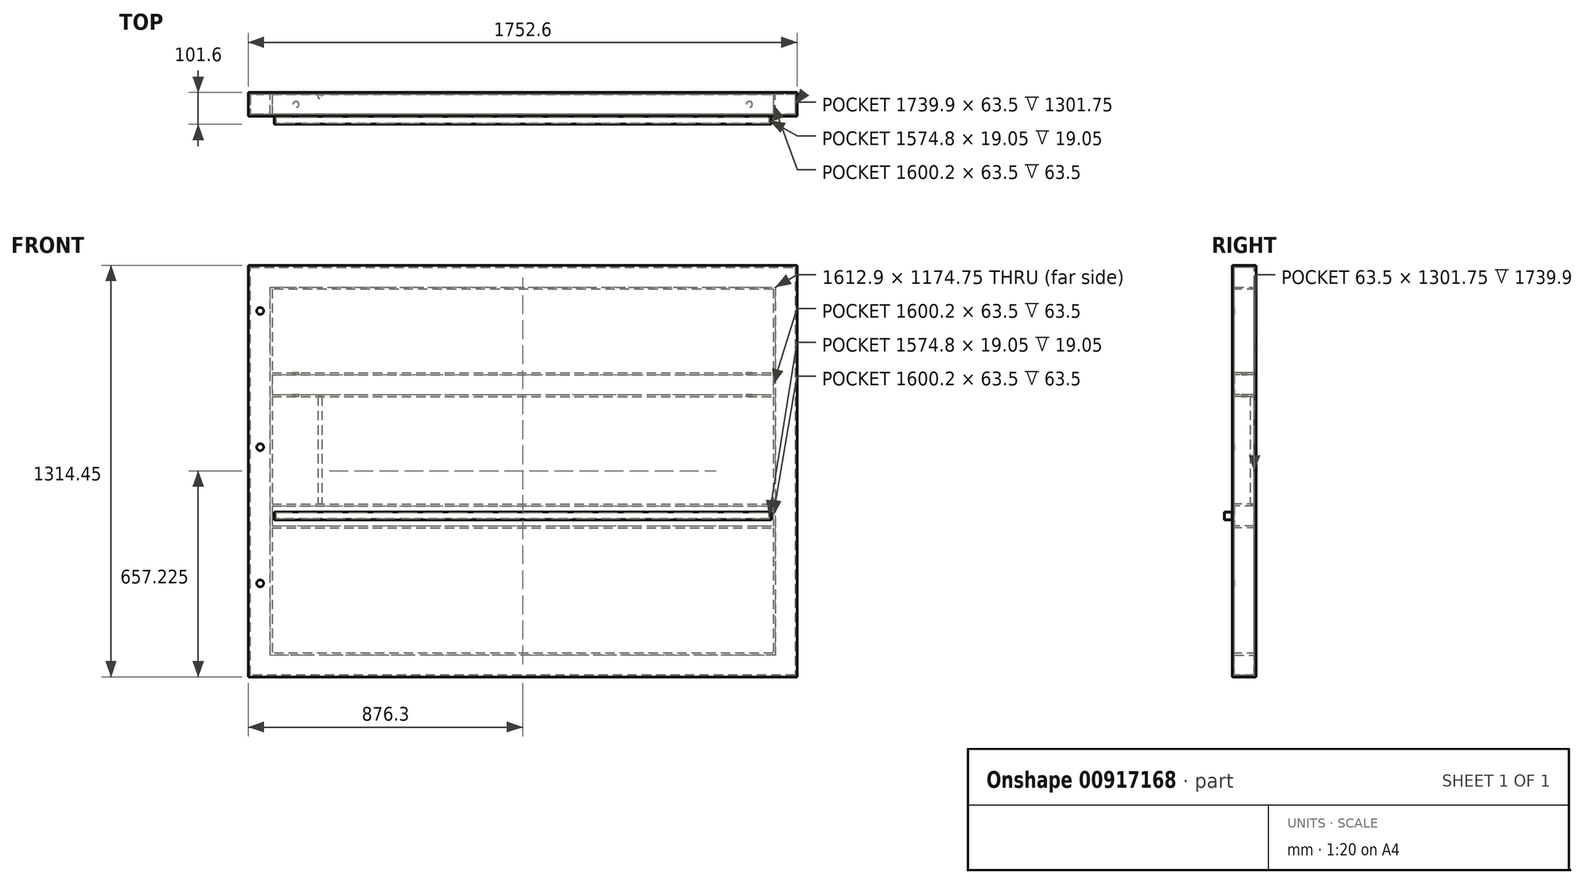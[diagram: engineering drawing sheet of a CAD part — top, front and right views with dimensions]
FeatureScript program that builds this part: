
annotation { "Feature Type Name" : "Feature", "Feature Type Description" : "" }
export const myFeature = defineFeature(function(context is Context, id is Id, definition is map)
    precondition{}
    {
        {
            var Q0;
            Q0=qCreatedBy(makeId("Front.planeOp"),FACE);
            var sketch = newSketch(context, id + "F0", { "sketchPlane" : qUnion([Q0])});
            skLineSegment(sketch, "E0.bottom", {"start": v(-876.3, 660.4) * mm, "end": v(876.3, 660.4) * mm});
            skLineSegment(sketch, "E0.top", {"start": v(-876.3, -654.05) * mm, "end": v(876.3, -654.05) * mm});
            skLineSegment(sketch, "E0.left", {"start": v(-876.3, 660.4) * mm, "end": v(-876.3, -654.05) * mm});
            skLineSegment(sketch, "E0.right", {"start": v(876.3, 660.4) * mm, "end": v(876.3, -654.05) * mm});
            skLineSegment(sketch, "E1.bottom", {"start": v(-800.1, 635) * mm, "end": v(800.1, 635) * mm, "construction": true});
            skLineSegment(sketch, "E1.top", {"start": v(-800.1, -603.25) * mm, "end": v(800.1, -603.25) * mm, "construction": true});
            skLineSegment(sketch, "E1.left", {"start": v(-800.1, 635) * mm, "end": v(-800.1, -603.25) * mm, "construction": true});
            skLineSegment(sketch, "E1.right", {"start": v(800.1, 635) * mm, "end": v(800.1, -603.25) * mm, "construction": true});
            skSolve(sketch);
        }
        {
            var Q0;
            Q0=qCreatedBy(makeId("Top.planeOp"),FACE);
            var sketch = newSketch(context, id + "F1", { "sketchPlane" : qUnion([Q0])});
            skLineSegment(sketch, "E2.bottom", {"start": v(-800.1, -76.2) * mm, "end": v(-876.3, -76.2) * mm});
            skLineSegment(sketch, "E2.top", {"start": v(-800.1, 0) * mm, "end": v(-876.3, 0) * mm});
            skLineSegment(sketch, "E2.left", {"start": v(-800.1, -76.2) * mm, "end": v(-800.1, 0) * mm});
            skLineSegment(sketch, "E2.right", {"start": v(-876.3, -76.2) * mm, "end": v(-876.3, 0) * mm});
            skPoint(sketch, "E2.middle", {"position": v(-838.2, -38.1) * mm});
            skLineSegment(sketch, "E3.bottom", {"start": v(-806.45, -69.85) * mm, "end": v(-869.95, -69.85) * mm});
            skLineSegment(sketch, "E3.top", {"start": v(-806.45, -6.35) * mm, "end": v(-869.95, -6.35) * mm});
            skLineSegment(sketch, "E3.left", {"start": v(-806.45, -69.85) * mm, "end": v(-806.45, -6.35) * mm});
            skLineSegment(sketch, "E3.right", {"start": v(-869.95, -69.85) * mm, "end": v(-869.95, -6.35) * mm});
            skSolve(sketch);
        }
        {
            var Q0;
            Q0=qSketchRegion(id+"F1",true);
            var Q1;
            Q1=qConstructionFilter(qBodyType(qCreatedBy(id+"F0",EDGE),BodyType.WIRE),ConstructionObject.NO);
            sweep(context, id + "F2", {"profiles" : qUnion([Q0]), "path" : qUnion([Q1])});
        }
        {
            var Q0;
            Q0=qCreatedBy(makeId("Right.planeOp"),FACE);
            var sketch = newSketch(context, id + "F3", { "sketchPlane" : qUnion([Q0])});
            skLineSegment(sketch, "E4.bottom", {"start": v(0, 736.6) * mm, "end": v(-76.2, 736.6) * mm, "construction": true});
            skLineSegment(sketch, "E4.top", {"start": v(0, 660.4) * mm, "end": v(-76.2, 660.4) * mm, "construction": true});
            skLineSegment(sketch, "E4.left", {"start": v(0, 736.6) * mm, "end": v(0, 660.4) * mm, "construction": true});
            skLineSegment(sketch, "E4.right", {"start": v(-76.2, 736.6) * mm, "end": v(-76.2, 660.4) * mm, "construction": true});
            skPoint(sketch, "E4.middle", {"position": v(-38.1, 698.5) * mm});
            skLineSegment(sketch, "E5.bottom", {"start": v(-6.35, 730.25) * mm, "end": v(-69.85, 730.25) * mm, "construction": true});
            skLineSegment(sketch, "E5.top", {"start": v(-6.35, 666.75) * mm, "end": v(-69.85, 666.75) * mm, "construction": true});
            skLineSegment(sketch, "E5.left", {"start": v(-6.35, 730.25) * mm, "end": v(-6.35, 666.75) * mm, "construction": true});
            skLineSegment(sketch, "E5.right", {"start": v(-69.85, 730.25) * mm, "end": v(-69.85, 666.75) * mm, "construction": true});
            skLineSegment(sketch, "E6.0.1.0", {"start": v(0, 317.5) * mm, "end": v(-76.2, 317.5) * mm});
            skLineSegment(sketch, "E6.0.1.1", {"start": v(0, 241.3) * mm, "end": v(-76.2, 241.3) * mm});
            skLineSegment(sketch, "E6.0.1.2", {"start": v(0, 317.5) * mm, "end": v(0, 241.3) * mm});
            skLineSegment(sketch, "E6.0.1.3", {"start": v(-76.2, 317.5) * mm, "end": v(-76.2, 241.3) * mm});
            skLineSegment(sketch, "E6.0.1.4", {"start": v(-6.35, 311.15) * mm, "end": v(-69.85, 311.15) * mm});
            skLineSegment(sketch, "E6.0.1.5", {"start": v(-6.35, 247.65) * mm, "end": v(-69.85, 247.65) * mm});
            skLineSegment(sketch, "E6.0.1.6", {"start": v(-6.35, 311.15) * mm, "end": v(-6.35, 247.65) * mm});
            skLineSegment(sketch, "E6.0.1.7", {"start": v(-69.85, 311.15) * mm, "end": v(-69.85, 247.65) * mm});
            skPoint(sketch, "E6.0.1.8", {"position": v(-38.1, 279.4) * mm});
            skPoint(sketch, "E6.0.1.9", {"position": v(-38.1, 279.4) * mm});
            skLineSegment(sketch, "E6.direction1", {"start": v(-76.2, 660.4) * mm, "end": v(586.54, 660.4) * mm, "construction": true});
            skLineSegment(sketch, "E6.direction2", {"start": v(-76.2, 660.4) * mm, "end": v(-76.2, 241.3) * mm, "construction": true});
            skLineSegment(sketch, "E7.0.0.2", {"start": v(0, -101.6) * mm, "end": v(-76.2, -101.6) * mm});
            skLineSegment(sketch, "E7.3.0.2", {"start": v(0, -177.8) * mm, "end": v(-76.2, -177.8) * mm});
            skLineSegment(sketch, "E7.6.0.2", {"start": v(0, -101.6) * mm, "end": v(0, -177.8) * mm});
            skLineSegment(sketch, "E7.9.0.2", {"start": v(-76.2, -101.6) * mm, "end": v(-76.2, -177.8) * mm});
            skLineSegment(sketch, "E7.12.0.2", {"start": v(-6.35, -107.95) * mm, "end": v(-69.85, -107.95) * mm});
            skLineSegment(sketch, "E7.15.0.2", {"start": v(-6.35, -171.45) * mm, "end": v(-69.85, -171.45) * mm});
            skLineSegment(sketch, "E7.18.0.2", {"start": v(-6.35, -107.95) * mm, "end": v(-6.35, -171.45) * mm});
            skLineSegment(sketch, "E7.21.0.2", {"start": v(-69.85, -107.95) * mm, "end": v(-69.85, -171.45) * mm});
            skPoint(sketch, "E7.24.0.2", {"position": v(-38.1, -139.7) * mm});
            skPoint(sketch, "E7.25.0.2", {"position": v(-38.1, -139.7) * mm});
            skLineSegment(sketch, "E8.0.0.3", {"start": v(0, -520.7) * mm, "end": v(-76.2, -520.7) * mm, "construction": true});
            skLineSegment(sketch, "E8.3.0.3", {"start": v(0, -596.9) * mm, "end": v(-76.2, -596.9) * mm, "construction": true});
            skLineSegment(sketch, "E8.6.0.3", {"start": v(0, -520.7) * mm, "end": v(0, -596.9) * mm, "construction": true});
            skLineSegment(sketch, "E8.9.0.3", {"start": v(-76.2, -520.7) * mm, "end": v(-76.2, -596.9) * mm, "construction": true});
            skLineSegment(sketch, "E8.12.0.3", {"start": v(-6.35, -527.05) * mm, "end": v(-69.85, -527.05) * mm, "construction": true});
            skLineSegment(sketch, "E8.15.0.3", {"start": v(-6.35, -590.55) * mm, "end": v(-69.85, -590.55) * mm, "construction": true});
            skLineSegment(sketch, "E8.18.0.3", {"start": v(-6.35, -527.05) * mm, "end": v(-6.35, -590.55) * mm, "construction": true});
            skLineSegment(sketch, "E8.21.0.3", {"start": v(-69.85, -527.05) * mm, "end": v(-69.85, -590.55) * mm, "construction": true});
            skPoint(sketch, "E8.24.0.3", {"position": v(-38.1, -558.8) * mm});
            skPoint(sketch, "E8.25.0.3", {"position": v(-38.1, -558.8) * mm});
            skLineSegment(sketch, "E9", {"start": v(-76.2, -673.1) * mm, "end": v(-76.2, -520.7) * mm, "construction": true});
            skLineSegment(sketch, "E10", {"start": v(-76.2, -520.7) * mm, "end": v(0, -520.7) * mm, "construction": true});
            skLineSegment(sketch, "E11", {"start": v(0, -520.7) * mm, "end": v(0, -527.05) * mm, "construction": true});
            skLineSegment(sketch, "E12", {"start": v(0, -527.05) * mm, "end": v(-69.85, -527.05) * mm, "construction": true});
            skLineSegment(sketch, "E13", {"start": v(-69.85, -527.05) * mm, "end": v(-69.85, -666.75) * mm, "construction": true});
            skLineSegment(sketch, "E14", {"start": v(-69.85, -666.75) * mm, "end": v(0, -666.75) * mm, "construction": true});
            skLineSegment(sketch, "E15", {"start": v(0, -666.75) * mm, "end": v(0, -673.1) * mm, "construction": true});
            skLineSegment(sketch, "E16", {"start": v(-76.2, -673.1) * mm, "end": v(0, -673.1) * mm, "construction": true});
            skLineSegment(sketch, "E17", {"start": v(-38.1, 660.4) * mm, "end": v(-38.1, 317.5) * mm, "construction": true});
            skLineSegment(sketch, "E18", {"start": v(-38.1, 317.5) * mm, "end": v(-38.1, 241.3) * mm, "construction": true});
            skLineSegment(sketch, "E19", {"start": v(-38.1, 241.3) * mm, "end": v(-38.1, -101.6) * mm, "construction": true});
            skLineSegment(sketch, "E20", {"start": v(-38.1, -101.6) * mm, "end": v(-38.1, -177.8) * mm, "construction": true});
            skLineSegment(sketch, "E21", {"start": v(-38.1, -177.8) * mm, "end": v(-38.1, -520.7) * mm, "construction": true});
            skLineSegment(sketch, "E22.bottom", {"start": v(-76.2, -596.9) * mm, "end": v(0, -596.9) * mm, "construction": true});
            skLineSegment(sketch, "E22.left", {"start": v(-76.2, -596.9) * mm, "end": v(-76.2, -673.1) * mm, "construction": true});
            skLineSegment(sketch, "E22.right", {"start": v(0, -596.9) * mm, "end": v(0, -673.1) * mm, "construction": true});
            skPoint(sketch, "E22.middle", {"position": v(-38.1, -635) * mm});
            skLineSegment(sketch, "E23.bottom", {"start": v(-6.35, -603.25) * mm, "end": v(-69.85, -603.25) * mm, "construction": true});
            skLineSegment(sketch, "E23.top", {"start": v(-6.35, -666.75) * mm, "end": v(-69.85, -666.75) * mm, "construction": true});
            skLineSegment(sketch, "E23.left", {"start": v(-6.35, -603.25) * mm, "end": v(-6.35, -666.75) * mm, "construction": true});
            skLineSegment(sketch, "E23.right", {"start": v(-69.85, -603.25) * mm, "end": v(-69.85, -666.75) * mm, "construction": true});
            skSolve(sketch);
        }
        {
            var Q0;
            Q0=qSketchRegion(id+"F3",true);
            var Q1;
            Q1=makeQuery(id+"F2.opSweep","SWEPT_FACE",FACE,{"disambiguationData":[OSD([sQuery(id+"F0.wireOp",EDGE,"E0.left"),sQuery(id+"F1.wireOp",EDGE,"E2.left")])]});
            var Q2;
            Q2=makeQuery(id+"F2.opSweep","CAP_VERTEX",VERTEX,{"disambiguationData":[OSD([sQuery(id+"F0.wireOp",EDGE,"E0.bottom"),sQuery(id+"F1.wireOp",EDGE,"E2.bottom"),sQuery(id+"F1.wireOp",EDGE,"E2.left")])],"isStart":true});
            var Q3;
            Q3=makeQuery(id+"F2.opSweep","SWEPT_FACE",FACE,{"disambiguationData":[OSD([sQuery(id+"F0.wireOp",EDGE,"E0.right"),sQuery(id+"F1.wireOp",EDGE,"E2.left")])]});
            var Q4;
            Q4=makeQuery(id+"F2.opSweep","MID_CAP_VERTEX",VERTEX,{"disambiguationData":[OSD([sQuery(id+"F0.wireOp",EDGE,"E0.bottom"),sQuery(id+"F1.wireOp",EDGE,"E2.bottom"),sQuery(id+"F1.wireOp",EDGE,"E2.left")])],"capPos":1.0});
            extrude(context, id + "F4", {"entities" : qUnion([Q0]), "operationType" : NewBodyOperationType.ADD, "endBound" : BoundingType.UP_TO_VERTEX, "oppositeDirection" : true, "depth" : 25.4 * mm, "endBoundEntityFace" : qUnion([Q1]), "endBoundEntityVertex" : qUnion([Q2]), "offsetDistance" : 25.4 * mm, "hasSecondDirection" : true, "secondDirectionBound" : SecondDirectionBoundingType.UP_TO_VERTEX, "secondDirectionOppositeDirection" : false, "secondDirectionDepth" : 25.4 * mm, "secondDirectionBoundEntityFace" : qUnion([Q3]), "secondDirectionBoundEntityVertex" : qUnion([Q4])});
        }
        {
            var Q0;
            Q0=qCreatedBy(makeId("Right.planeOp"),FACE);
            var sketch = newSketch(context, id + "F5", { "sketchPlane" : qUnion([Q0])});
            skLineSegment(sketch, "E24.bottom", {"start": v(-76.2, -127) * mm, "end": v(-101.6, -127) * mm});
            skLineSegment(sketch, "E24.top", {"start": v(-76.2, -152.4) * mm, "end": v(-101.6, -152.4) * mm});
            skLineSegment(sketch, "E24.left", {"start": v(-76.2, -127) * mm, "end": v(-76.2, -152.4) * mm});
            skLineSegment(sketch, "E24.right", {"start": v(-101.6, -127) * mm, "end": v(-101.6, -152.4) * mm});
            skPoint(sketch, "E24.middle", {"position": v(-88.9, -139.7) * mm});
            skLineSegment(sketch, "E25.bottom", {"start": v(-79.37, -130.17) * mm, "end": v(-98.42, -130.17) * mm});
            skLineSegment(sketch, "E25.top", {"start": v(-79.37, -149.22) * mm, "end": v(-98.42, -149.22) * mm});
            skLineSegment(sketch, "E25.left", {"start": v(-79.37, -130.17) * mm, "end": v(-79.37, -149.22) * mm});
            skLineSegment(sketch, "E25.right", {"start": v(-98.42, -130.17) * mm, "end": v(-98.42, -149.22) * mm});
            skSolve(sketch);
        }
        {
            var Q0;
            Q0=qSketchRegion(id+"F5",true);
            extrude(context, id + "F6", {"entities" : qUnion([Q0]), "operationType" : NewBodyOperationType.ADD, "endBound" : BoundingType.SYMMETRIC, "depth" : 1587.5 * mm, "offsetDistance" : 25.4 * mm});
        }
        {
            var Q0;
            Q0=makeQuery(id+"F6.opExtrude","SWEPT_FACE",FACE,{"disambiguationData":[OSD([sQuery(id+"F5.wireOp",EDGE,"E24.bottom")])]});
            var sketch = newSketch(context, id + "F7", { "sketchPlane" : qUnion([Q0])});
            skLineSegment(sketch, "E26.bottom", {"start": v(793.75, -76.2) * mm, "end": v(787.4, -76.2) * mm});
            skLineSegment(sketch, "E26.top", {"start": v(793.75, -101.6) * mm, "end": v(787.4, -101.6) * mm});
            skLineSegment(sketch, "E26.left", {"start": v(793.75, -76.2) * mm, "end": v(793.75, -101.6) * mm});
            skLineSegment(sketch, "E26.right", {"start": v(787.4, -76.2) * mm, "end": v(787.4, -101.6) * mm});
            skLineSegment(sketch, "E27.bottom", {"start": v(-793.75, -76.2) * mm, "end": v(-787.4, -76.2) * mm});
            skLineSegment(sketch, "E27.top", {"start": v(-793.75, -101.6) * mm, "end": v(-787.4, -101.6) * mm});
            skLineSegment(sketch, "E27.left", {"start": v(-793.75, -76.2) * mm, "end": v(-793.75, -101.6) * mm});
            skLineSegment(sketch, "E27.right", {"start": v(-787.4, -76.2) * mm, "end": v(-787.4, -101.6) * mm});
            skSolve(sketch);
        }
        {
            var Q0;
            Q0=qSketchRegion(id+"F7",true);
            var Q1;
            Q1=makeQuery(id+"F6.opExtrude","CAP_VERTEX",VERTEX,{"disambiguationData":[OSD([sQuery(id+"F5.wireOp",EDGE,"E24.top"),sQuery(id+"F5.wireOp",EDGE,"E24.right")])],"isStart":false});
            extrude(context, id + "F8", {"entities" : qUnion([Q0]), "operationType" : NewBodyOperationType.ADD, "endBound" : BoundingType.UP_TO_VERTEX, "oppositeDirection" : true, "depth" : 25.4 * mm, "endBoundEntityVertex" : qUnion([Q1]), "offsetDistance" : 25.4 * mm});
        }
        {
            var Q0;
            Q0=qCreatedBy(makeId("Top.planeOp"),FACE);
            var sketch = newSketch(context, id + "F9", { "sketchPlane" : qUnion([Q0])});
            skLineSegment(sketch, "E28.bottom", {"start": v(800.1, -76.2) * mm, "end": v(-800.1, -76.2) * mm});
            skLineSegment(sketch, "E28.top", {"start": v(800.1, -73.53) * mm, "end": v(-800.1, -73.53) * mm});
            skLineSegment(sketch, "E28.left", {"start": v(800.1, -76.2) * mm, "end": v(800.1, -73.53) * mm});
            skLineSegment(sketch, "E28.right", {"start": v(-800.1, -76.2) * mm, "end": v(-800.1, -73.53) * mm});
            skPoint(sketch, "E28.middle", {"position": v(0, -74.87) * mm});
            skSolve(sketch);
        }
        {
            var Q0;
            Q0=qSketchRegion(id+"F9",true);
            var Q1;
            Q1=makeQuery(id+"F2.opSweep","CAP_VERTEX",VERTEX,{"disambiguationData":[OSD([sQuery(id+"F0.wireOp",EDGE,"E0.bottom"),sQuery(id+"F1.wireOp",EDGE,"E2.top"),sQuery(id+"F1.wireOp",EDGE,"E2.left")])],"isStart":true});
            var Q2;
            Q2=makeQuery(id+"F2.opSweep","MID_CAP_VERTEX",VERTEX,{"disambiguationData":[OSD([sQuery(id+"F0.wireOp",EDGE,"E0.left"),sQuery(id+"F1.wireOp",EDGE,"E2.top"),sQuery(id+"F1.wireOp",EDGE,"E2.left")])],"capPos":3.0});
            extrude(context, id + "F10", {"entities" : qUnion([Q0]), "operationType" : NewBodyOperationType.ADD, "endBound" : BoundingType.UP_TO_VERTEX, "depth" : 25.4 * mm, "endBoundEntityVertex" : qUnion([Q1]), "offsetDistance" : 25.4 * mm, "hasSecondDirection" : true, "secondDirectionBound" : SecondDirectionBoundingType.UP_TO_VERTEX, "secondDirectionOppositeDirection" : true, "secondDirectionDepth" : 25.4 * mm, "secondDirectionBoundEntityVertex" : qUnion([Q2])});
        }
        {
            var Q0;
            Q0=qCreatedBy(makeId("Front.planeOp"),FACE);
            var sketch = newSketch(context, id + "F11", { "sketchPlane" : qUnion([Q0])});
            skCircle(sketch, "E29", {"center": v(-838.2, 514.35) * mm, "radius": 11.11 * mm});
            skCircle(sketch, "E30", {"center": v(-838.2, 79.37) * mm, "radius": 11.11 * mm});
            skCircle(sketch, "E31", {"center": v(-838.2, -355.6) * mm, "radius": 11.11 * mm});
            skLineSegment(sketch, "E32", {"start": v(-838.2, 79.37) * mm, "end": v(-838.2, -355.6) * mm, "construction": true});
            skLineSegment(sketch, "E33", {"start": v(-838.2, 514.35) * mm, "end": v(-838.2, 79.37) * mm, "construction": true});
            skLineSegment(sketch, "E34", {"start": v(-838.2, 660.4) * mm, "end": v(-838.2, 514.35) * mm, "construction": true});
            skLineSegment(sketch, "E35", {"start": v(-838.2, -355.6) * mm, "end": v(-838.2, -501.65) * mm, "construction": true});
            skLineSegment(sketch, "E36", {"start": v(-838.2, 514.35) * mm, "end": v(-838.2, 296.86) * mm, "construction": true});
            skLineSegment(sketch, "E37", {"start": v(-800.1, 514.35) * mm, "end": v(-838.2, 514.35) * mm, "construction": true});
            skLineSegment(sketch, "E38", {"start": v(-838.2, 514.35) * mm, "end": v(-876.3, 514.35) * mm, "construction": true});
            skLineSegment(sketch, "E39", {"start": v(-838.2, -501.65) * mm, "end": v(-838.2, -654.05) * mm, "construction": true});
            skSolve(sketch);
        }
        {
            var Q0;
            Q0=qSketchRegion(id+"F11",true);
            extrude(context, id + "F12", {"entities" : qUnion([Q0]), "operationType" : NewBodyOperationType.REMOVE, "endBound" : BoundingType.THROUGH_ALL, "depth" : 25.4 * mm, "offsetDistance" : 25.4 * mm});
        }
        {
            var Q0;
            Q0=makeQuery(id+"F4.opExtrude","SWEPT_FACE",FACE,{"disambiguationData":[OSD([sQuery(id+"F3.wireOp",EDGE,"E6.0.1.0")])]});
            var sketch = newSketch(context, id + "F13", { "sketchPlane" : qUnion([Q0])});
            skCircle(sketch, "E40", {"center": v(-723.9, -38.1) * mm, "radius": 9.53 * mm});
            skLineSegment(sketch, "E41", {"start": v(-723.9, -38.1) * mm, "end": v(0, -38.1) * mm, "construction": true});
            skLineSegment(sketch, "E42", {"start": v(-723.9, -762) * mm, "end": v(-723.9, -38.1) * mm, "construction": true});
            skLineSegment(sketch, "E43", {"start": v(-723.9, 60.36) * mm, "end": v(-723.9, -38.1) * mm, "construction": true});
            skLineSegment(sketch, "E44", {"start": v(-723.9, 0) * mm, "end": v(-723.9, -38.1) * mm, "construction": true});
            skLineSegment(sketch, "E45", {"start": v(-819.15, 0) * mm, "end": v(-723.9, 0) * mm, "construction": true});
            skLineSegment(sketch, "E46", {"start": v(0, -76.2) * mm, "end": v(0, 0) * mm, "construction": true});
            skCircle(sketch, "E47.MirrorC", {"center": v(723.9, -38.1) * mm, "radius": 9.53 * mm});
            skSolve(sketch);
        }
        {
            var Q0;
            Q0=qSketchRegion(id+"F13",true);
            var Q1;
            Q1=makeQuery(id+"F4.opExtrude","SWEPT_FACE",FACE,{"disambiguationData":[OSD([sQuery(id+"F3.wireOp",EDGE,"E6.0.1.1")])]});
            extrude(context, id + "F14", {"entities" : qUnion([Q0]), "operationType" : NewBodyOperationType.REMOVE, "endBound" : BoundingType.UP_TO_SURFACE, "oppositeDirection" : true, "depth" : 25.4 * mm, "endBoundEntityFace" : qUnion([Q1]), "offsetDistance" : 25.4 * mm});
        }
        {
            var Q0;
            Q0=qCreatedBy(makeId("Top.planeOp"),FACE);
            var sketch = newSketch(context, id + "F15", { "sketchPlane" : qUnion([Q0])});
            skCircle(sketch, "E48", {"center": v(-647.7, -12.7) * mm, "radius": 6.35 * mm});
            skLineSegment(sketch, "E49", {"start": v(-647.7, -12.7) * mm, "end": v(-647.7, -73.53) * mm, "construction": true});
            skLineSegment(sketch, "E50", {"start": v(-647.7, 0) * mm, "end": v(-647.7, -12.7) * mm, "construction": true});
            skSolve(sketch);
        }
        {
            var Q0;
            Q0=qSketchRegion(id+"F15",true);
            extrude(context, id + "F16", {"entities" : qUnion([Q0]), "operationType" : NewBodyOperationType.ADD, "endBound" : BoundingType.UP_TO_NEXT, "depth" : 25.4 * mm, "offsetDistance" : 25.4 * mm, "hasSecondDirection" : true, "secondDirectionBound" : SecondDirectionBoundingType.UP_TO_NEXT, "secondDirectionOppositeDirection" : true, "secondDirectionDepth" : 25.4 * mm});
        }
    });
